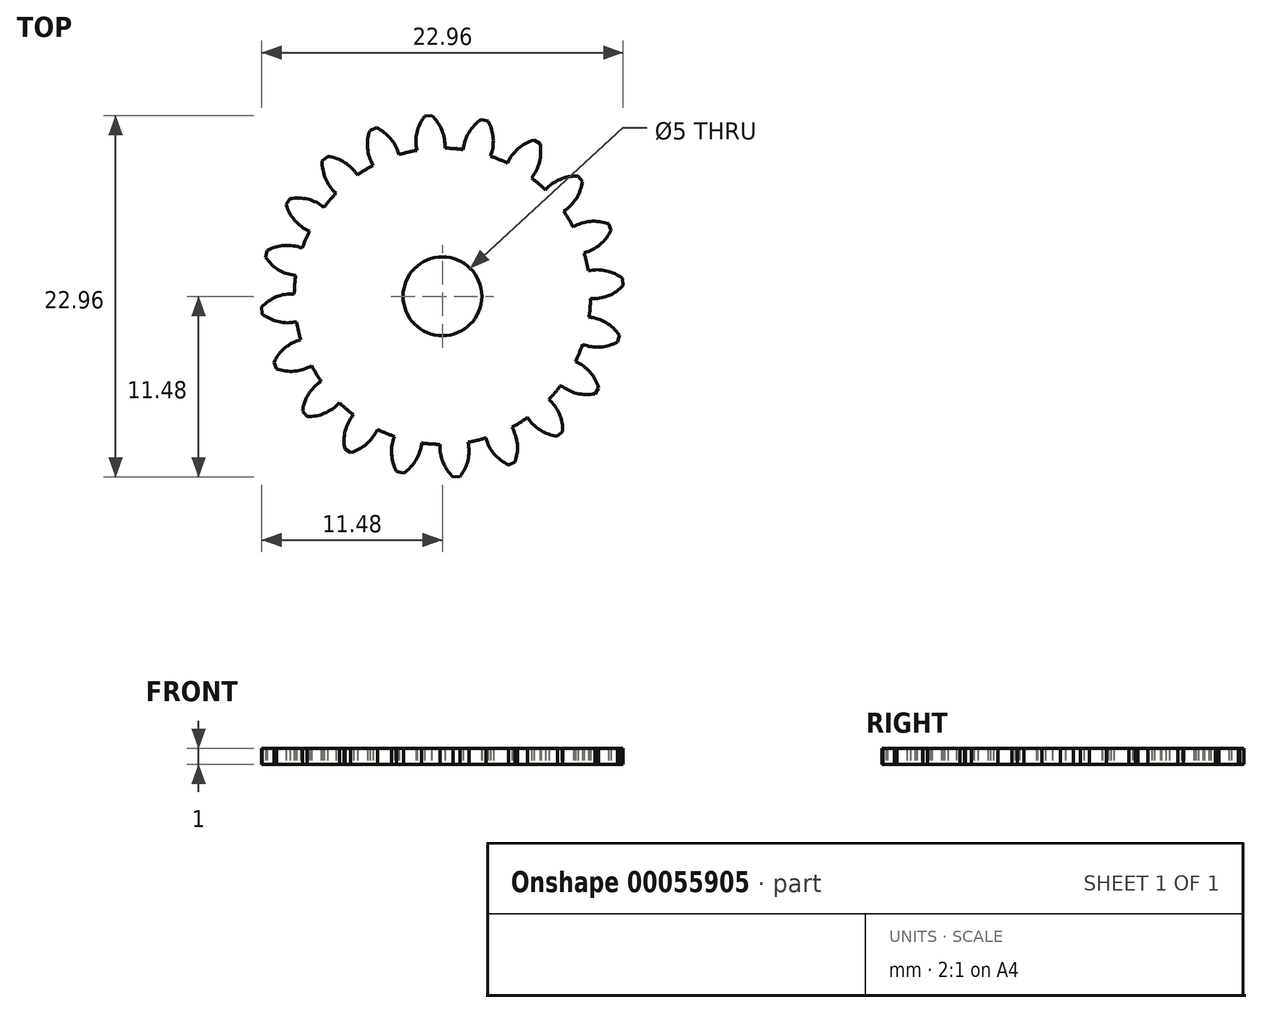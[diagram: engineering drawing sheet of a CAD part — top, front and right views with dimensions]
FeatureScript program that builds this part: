
annotation { "Feature Type Name" : "Feature", "Feature Type Description" : "" }
export const myFeature = defineFeature(function(context is Context, id is Id, definition is map)
    precondition{}
    {
        {
            assignVariable(context, id + "F0", {"name" : "GearDepth", "anyValue" : 1});
        }
        {
            var Q0;
            Q0=qCreatedBy(makeId("Top.planeOp"),FACE);
            var sketch = newSketch(context, id + "F1", { "sketchPlane" : qUnion([Q0])});
            skCircle(sketch, "E0", {"center": v(0, 0) * mm, "radius": 9.4 * mm});
            skCircle(sketch, "E1", {"center": v(0, 0) * mm, "radius": 10.45 * mm, "construction": true});
            skCircle(sketch, "E2", {"center": v(0, 0) * mm, "radius": 11.5 * mm, "construction": true});
            skLineSegment(sketch, "E3", {"start": v(0, 0) * mm, "end": v(0, 17.6) * mm, "construction": true});
            skLineSegment(sketch, "E4", {"start": v(0, 0) * mm, "end": v(-1.42, 18) * mm, "construction": true});
            skLineSegment(sketch, "E5", {"start": v(0, 10.45) * mm, "end": v(-10.54, 10.45) * mm, "construction": true});
            skLineSegment(sketch, "E6", {"start": v(0, 10.45) * mm, "end": v(-10.3, 6.7) * mm, "construction": true});
            skCircle(sketch, "E7", {"center": v(0, 10.45) * mm, "radius": 2.61 * mm, "construction": true});
            skCircle(sketch, "E8", {"center": v(-2.46, 9.56) * mm, "radius": 2.61 * mm, "construction": true});
            skArc(sketch, "E9", {"start": v(-4.91, 10.45) * mm, "mid": v(-4.92, 10.42) * mm, "end": v(-4.94, 10.39) * mm});
            skArc(sketch, "E10.trimOffspring", {"start": v(0.15, 9.4) * mm, "mid": v(-0.03, 10.54) * mm, "end": v(-0.68, 11.48) * mm});
            skArc(sketch, "E11.MirrorCS", {"start": v(-1.62, 9.27) * mm, "mid": v(-1.62, 10.41) * mm, "end": v(-1.12, 11.45) * mm});
            skLineSegment(sketch, "E12", {"start": v(-1.12, 11.45) * mm, "end": v(-0.68, 11.48) * mm});
            skArc(sketch, "E13.1.0", {"start": v(-2.76, 9) * mm, "mid": v(-3.29, 10.01) * mm, "end": v(-4.2, 10.7) * mm});
            skLineSegment(sketch, "E13.1.1", {"start": v(-4.6, 10.54) * mm, "end": v(-4.2, 10.7) * mm});
            skArc(sketch, "E13.1.2", {"start": v(-4.4, 8.31) * mm, "mid": v(-4.76, 9.4) * mm, "end": v(-4.6, 10.54) * mm});
            skArc(sketch, "E13.2.0", {"start": v(-5.4, 7.7) * mm, "mid": v(-6.22, 8.5) * mm, "end": v(-7.3, 8.89) * mm});
            skLineSegment(sketch, "E13.2.1", {"start": v(-7.64, 8.6) * mm, "end": v(-7.3, 8.89) * mm});
            skArc(sketch, "E13.2.2", {"start": v(-6.76, 6.54) * mm, "mid": v(-7.43, 7.47) * mm, "end": v(-7.64, 8.6) * mm});
            skArc(sketch, "E13.3.0", {"start": v(-7.52, 5.65) * mm, "mid": v(-8.54, 6.17) * mm, "end": v(-9.69, 6.2) * mm});
            skLineSegment(sketch, "E13.3.1", {"start": v(-9.92, 5.82) * mm, "end": v(-9.69, 6.2) * mm});
            skArc(sketch, "E13.3.2", {"start": v(-8.45, 4.13) * mm, "mid": v(-9.37, 4.81) * mm, "end": v(-9.92, 5.82) * mm});
            skArc(sketch, "E13.4.0", {"start": v(-8.9, 3.05) * mm, "mid": v(-10.03, 3.23) * mm, "end": v(-11.13, 2.9) * mm});
            skLineSegment(sketch, "E13.4.1", {"start": v(-11.23, 2.47) * mm, "end": v(-11.13, 2.9) * mm});
            skArc(sketch, "E13.4.2", {"start": v(-9.32, 1.32) * mm, "mid": v(-10.4, 1.68) * mm, "end": v(-11.23, 2.47) * mm});
            skArc(sketch, "E13.5.0", {"start": v(-9.4, 0.15) * mm, "mid": v(-10.54, -0.03) * mm, "end": v(-11.48, -0.68) * mm});
            skLineSegment(sketch, "E13.5.1", {"start": v(-11.45, -1.12) * mm, "end": v(-11.48, -0.68) * mm});
            skArc(sketch, "E13.5.2", {"start": v(-9.27, -1.62) * mm, "mid": v(-10.41, -1.62) * mm, "end": v(-11.45, -1.12) * mm});
            skArc(sketch, "E13.6.0", {"start": v(-9, -2.76) * mm, "mid": v(-10.01, -3.29) * mm, "end": v(-10.7, -4.2) * mm});
            skLineSegment(sketch, "E13.6.1", {"start": v(-10.54, -4.6) * mm, "end": v(-10.7, -4.2) * mm});
            skArc(sketch, "E13.6.2", {"start": v(-8.31, -4.4) * mm, "mid": v(-9.4, -4.76) * mm, "end": v(-10.54, -4.6) * mm});
            skArc(sketch, "E13.7.0", {"start": v(-7.7, -5.4) * mm, "mid": v(-8.5, -6.22) * mm, "end": v(-8.89, -7.3) * mm});
            skLineSegment(sketch, "E13.7.1", {"start": v(-8.6, -7.64) * mm, "end": v(-8.89, -7.3) * mm});
            skArc(sketch, "E13.7.2", {"start": v(-6.54, -6.76) * mm, "mid": v(-7.47, -7.43) * mm, "end": v(-8.6, -7.64) * mm});
            skArc(sketch, "E13.8.0", {"start": v(-5.65, -7.52) * mm, "mid": v(-6.17, -8.54) * mm, "end": v(-6.2, -9.69) * mm});
            skLineSegment(sketch, "E13.8.1", {"start": v(-5.82, -9.92) * mm, "end": v(-6.2, -9.69) * mm});
            skArc(sketch, "E13.8.2", {"start": v(-4.13, -8.45) * mm, "mid": v(-4.81, -9.37) * mm, "end": v(-5.82, -9.92) * mm});
            skArc(sketch, "E13.9.0", {"start": v(-3.05, -8.9) * mm, "mid": v(-3.23, -10.03) * mm, "end": v(-2.9, -11.13) * mm});
            skLineSegment(sketch, "E13.9.1", {"start": v(-2.47, -11.23) * mm, "end": v(-2.9, -11.13) * mm});
            skArc(sketch, "E13.9.2", {"start": v(-1.32, -9.32) * mm, "mid": v(-1.68, -10.4) * mm, "end": v(-2.47, -11.23) * mm});
            skArc(sketch, "E13.10.0", {"start": v(-0.15, -9.4) * mm, "mid": v(0.03, -10.54) * mm, "end": v(0.68, -11.48) * mm});
            skLineSegment(sketch, "E13.10.1", {"start": v(1.12, -11.45) * mm, "end": v(0.68, -11.48) * mm});
            skArc(sketch, "E13.10.2", {"start": v(1.62, -9.27) * mm, "mid": v(1.62, -10.41) * mm, "end": v(1.12, -11.45) * mm});
            skArc(sketch, "E13.11.0", {"start": v(2.76, -9) * mm, "mid": v(3.29, -10.01) * mm, "end": v(4.2, -10.7) * mm});
            skLineSegment(sketch, "E13.11.1", {"start": v(4.6, -10.54) * mm, "end": v(4.2, -10.7) * mm});
            skArc(sketch, "E13.11.2", {"start": v(4.4, -8.31) * mm, "mid": v(4.76, -9.4) * mm, "end": v(4.6, -10.54) * mm});
            skArc(sketch, "E13.12.0", {"start": v(5.4, -7.7) * mm, "mid": v(6.22, -8.5) * mm, "end": v(7.3, -8.89) * mm});
            skLineSegment(sketch, "E13.12.1", {"start": v(7.64, -8.6) * mm, "end": v(7.3, -8.89) * mm});
            skArc(sketch, "E13.12.2", {"start": v(6.76, -6.54) * mm, "mid": v(7.43, -7.47) * mm, "end": v(7.64, -8.6) * mm});
            skArc(sketch, "E13.13.0", {"start": v(7.52, -5.65) * mm, "mid": v(8.54, -6.17) * mm, "end": v(9.69, -6.2) * mm});
            skLineSegment(sketch, "E13.13.1", {"start": v(9.92, -5.82) * mm, "end": v(9.69, -6.2) * mm});
            skArc(sketch, "E13.13.2", {"start": v(8.45, -4.13) * mm, "mid": v(9.37, -4.81) * mm, "end": v(9.92, -5.82) * mm});
            skArc(sketch, "E13.14.0", {"start": v(8.9, -3.05) * mm, "mid": v(10.03, -3.23) * mm, "end": v(11.13, -2.9) * mm});
            skLineSegment(sketch, "E13.14.1", {"start": v(11.23, -2.47) * mm, "end": v(11.13, -2.9) * mm});
            skArc(sketch, "E13.14.2", {"start": v(9.32, -1.32) * mm, "mid": v(10.4, -1.68) * mm, "end": v(11.23, -2.47) * mm});
            skArc(sketch, "E13.15.0", {"start": v(9.4, -0.15) * mm, "mid": v(10.54, 0.03) * mm, "end": v(11.48, 0.68) * mm});
            skLineSegment(sketch, "E13.15.1", {"start": v(11.45, 1.12) * mm, "end": v(11.48, 0.68) * mm});
            skArc(sketch, "E13.15.2", {"start": v(9.27, 1.62) * mm, "mid": v(10.41, 1.62) * mm, "end": v(11.45, 1.12) * mm});
            skArc(sketch, "E13.16.0", {"start": v(9, 2.76) * mm, "mid": v(10.01, 3.29) * mm, "end": v(10.7, 4.2) * mm});
            skLineSegment(sketch, "E13.16.1", {"start": v(10.54, 4.6) * mm, "end": v(10.7, 4.2) * mm});
            skArc(sketch, "E13.16.2", {"start": v(8.31, 4.4) * mm, "mid": v(9.4, 4.76) * mm, "end": v(10.54, 4.6) * mm});
            skArc(sketch, "E13.17.0", {"start": v(7.7, 5.4) * mm, "mid": v(8.5, 6.22) * mm, "end": v(8.89, 7.3) * mm});
            skLineSegment(sketch, "E13.17.1", {"start": v(8.6, 7.64) * mm, "end": v(8.89, 7.3) * mm});
            skArc(sketch, "E13.17.2", {"start": v(6.54, 6.76) * mm, "mid": v(7.47, 7.43) * mm, "end": v(8.6, 7.64) * mm});
            skArc(sketch, "E13.18.0", {"start": v(5.65, 7.52) * mm, "mid": v(6.17, 8.54) * mm, "end": v(6.2, 9.69) * mm});
            skLineSegment(sketch, "E13.18.1", {"start": v(5.82, 9.92) * mm, "end": v(6.2, 9.69) * mm});
            skArc(sketch, "E13.18.2", {"start": v(4.13, 8.45) * mm, "mid": v(4.81, 9.37) * mm, "end": v(5.82, 9.92) * mm});
            skArc(sketch, "E13.19.0", {"start": v(3.05, 8.9) * mm, "mid": v(3.23, 10.03) * mm, "end": v(2.9, 11.13) * mm});
            skLineSegment(sketch, "E13.19.1", {"start": v(2.47, 11.23) * mm, "end": v(2.9, 11.13) * mm});
            skArc(sketch, "E13.19.2", {"start": v(1.32, 9.32) * mm, "mid": v(1.68, 10.4) * mm, "end": v(2.47, 11.23) * mm});
            skCircle(sketch, "E14", {"center": v(0, 0) * mm, "radius": 2.5 * mm});
            skSolve(sketch);
        }
        {
            var Q0;
            {var subQ0=sQuery(id+"F1.wireOp",EDGE,"E10.trimOffspring");Q0=makeQuery(id+"F1.imprint","IMPRINT",FACE,{"disambiguationData":[TD([[makeQuery(id+"F1.imprint","IMPRINT",EDGE,{"derivedFrom":subQ0}),1.0]])]});}
            var Q1;
            {var subQ0=sQuery(id+"F1.wireOp",EDGE,"E0");var subQ1=makeQuery(id+"F1.imprint","INTERSECT",VERTEX,{"derivedFrom":[subQ0,sQuery(id+"F1.wireOp",EDGE,"E10.trimOffspring")]});Q1=makeQuery(id+"F1.imprint","IMPRINT",FACE,{"disambiguationData":[TD([[makeQuery(id+"F1.imprint","IMPRINT",EDGE,{"disambiguationData":[TD([[subQ1,-1.0]])],"derivedFrom":subQ0}),1.0]])]});}
            var Q2;
            {var subQ0=sQuery(id+"F1.wireOp",EDGE,"E13.1.0");Q2=makeQuery(id+"F1.imprint","IMPRINT",FACE,{"disambiguationData":[TD([[makeQuery(id+"F1.imprint","IMPRINT",EDGE,{"derivedFrom":subQ0}),1.0]])]});}
            var Q3;
            {var subQ0=sQuery(id+"F1.wireOp",EDGE,"E13.2.0");Q3=makeQuery(id+"F1.imprint","IMPRINT",FACE,{"disambiguationData":[TD([[makeQuery(id+"F1.imprint","IMPRINT",EDGE,{"derivedFrom":subQ0}),1.0]])]});}
            var Q4;
            {var subQ0=sQuery(id+"F1.wireOp",EDGE,"E13.3.0");Q4=makeQuery(id+"F1.imprint","IMPRINT",FACE,{"disambiguationData":[TD([[makeQuery(id+"F1.imprint","IMPRINT",EDGE,{"derivedFrom":subQ0}),1.0]])]});}
            var Q5;
            {var subQ0=sQuery(id+"F1.wireOp",EDGE,"E13.4.0");Q5=makeQuery(id+"F1.imprint","IMPRINT",FACE,{"disambiguationData":[TD([[makeQuery(id+"F1.imprint","IMPRINT",EDGE,{"derivedFrom":subQ0}),1.0]])]});}
            var Q6;
            {var subQ0=sQuery(id+"F1.wireOp",EDGE,"E13.5.0");Q6=makeQuery(id+"F1.imprint","IMPRINT",FACE,{"disambiguationData":[TD([[makeQuery(id+"F1.imprint","IMPRINT",EDGE,{"derivedFrom":subQ0}),1.0]])]});}
            var Q7;
            {var subQ0=sQuery(id+"F1.wireOp",EDGE,"E13.6.0");Q7=makeQuery(id+"F1.imprint","IMPRINT",FACE,{"disambiguationData":[TD([[makeQuery(id+"F1.imprint","IMPRINT",EDGE,{"derivedFrom":subQ0}),1.0]])]});}
            var Q8;
            {var subQ0=sQuery(id+"F1.wireOp",EDGE,"E13.7.0");Q8=makeQuery(id+"F1.imprint","IMPRINT",FACE,{"disambiguationData":[TD([[makeQuery(id+"F1.imprint","IMPRINT",EDGE,{"derivedFrom":subQ0}),1.0]])]});}
            var Q9;
            {var subQ0=sQuery(id+"F1.wireOp",EDGE,"E13.8.0");Q9=makeQuery(id+"F1.imprint","IMPRINT",FACE,{"disambiguationData":[TD([[makeQuery(id+"F1.imprint","IMPRINT",EDGE,{"derivedFrom":subQ0}),1.0]])]});}
            var Q10;
            {var subQ0=sQuery(id+"F1.wireOp",EDGE,"E13.9.0");Q10=makeQuery(id+"F1.imprint","IMPRINT",FACE,{"disambiguationData":[TD([[makeQuery(id+"F1.imprint","IMPRINT",EDGE,{"derivedFrom":subQ0}),1.0]])]});}
            var Q11;
            {var subQ0=sQuery(id+"F1.wireOp",EDGE,"E13.10.0");Q11=makeQuery(id+"F1.imprint","IMPRINT",FACE,{"disambiguationData":[TD([[makeQuery(id+"F1.imprint","IMPRINT",EDGE,{"derivedFrom":subQ0}),1.0]])]});}
            var Q12;
            {var subQ0=sQuery(id+"F1.wireOp",EDGE,"E13.11.0");Q12=makeQuery(id+"F1.imprint","IMPRINT",FACE,{"disambiguationData":[TD([[makeQuery(id+"F1.imprint","IMPRINT",EDGE,{"derivedFrom":subQ0}),1.0]])]});}
            var Q13;
            {var subQ0=sQuery(id+"F1.wireOp",EDGE,"E13.12.0");Q13=makeQuery(id+"F1.imprint","IMPRINT",FACE,{"disambiguationData":[TD([[makeQuery(id+"F1.imprint","IMPRINT",EDGE,{"derivedFrom":subQ0}),1.0]])]});}
            var Q14;
            {var subQ0=sQuery(id+"F1.wireOp",EDGE,"E13.13.0");Q14=makeQuery(id+"F1.imprint","IMPRINT",FACE,{"disambiguationData":[TD([[makeQuery(id+"F1.imprint","IMPRINT",EDGE,{"derivedFrom":subQ0}),1.0]])]});}
            var Q15;
            {var subQ0=sQuery(id+"F1.wireOp",EDGE,"E13.14.0");Q15=makeQuery(id+"F1.imprint","IMPRINT",FACE,{"disambiguationData":[TD([[makeQuery(id+"F1.imprint","IMPRINT",EDGE,{"derivedFrom":subQ0}),1.0]])]});}
            var Q16;
            {var subQ0=sQuery(id+"F1.wireOp",EDGE,"E13.15.0");Q16=makeQuery(id+"F1.imprint","IMPRINT",FACE,{"disambiguationData":[TD([[makeQuery(id+"F1.imprint","IMPRINT",EDGE,{"derivedFrom":subQ0}),1.0]])]});}
            var Q17;
            {var subQ0=sQuery(id+"F1.wireOp",EDGE,"E13.16.0");Q17=makeQuery(id+"F1.imprint","IMPRINT",FACE,{"disambiguationData":[TD([[makeQuery(id+"F1.imprint","IMPRINT",EDGE,{"derivedFrom":subQ0}),1.0]])]});}
            var Q18;
            {var subQ0=sQuery(id+"F1.wireOp",EDGE,"E13.17.0");Q18=makeQuery(id+"F1.imprint","IMPRINT",FACE,{"disambiguationData":[TD([[makeQuery(id+"F1.imprint","IMPRINT",EDGE,{"derivedFrom":subQ0}),1.0]])]});}
            var Q19;
            {var subQ0=sQuery(id+"F1.wireOp",EDGE,"E13.18.0");Q19=makeQuery(id+"F1.imprint","IMPRINT",FACE,{"disambiguationData":[TD([[makeQuery(id+"F1.imprint","IMPRINT",EDGE,{"derivedFrom":subQ0}),1.0]])]});}
            var Q20;
            {var subQ0=sQuery(id+"F1.wireOp",EDGE,"E13.19.0");Q20=makeQuery(id+"F1.imprint","IMPRINT",FACE,{"disambiguationData":[TD([[makeQuery(id+"F1.imprint","IMPRINT",EDGE,{"derivedFrom":subQ0}),1.0]])]});}
            var Q21;
            Q21=sQuery(id+"F1.wireOp",EDGE,"E0");
            var Q22;
            Q22=sQuery(id+"F1.wireOp",EDGE,"E10.trimOffspring");
            var Q23;
            Q23=sQuery(id+"F1.wireOp",EDGE,"E12");
            var Q24;
            Q24=sQuery(id+"F1.wireOp",EDGE,"E11.MirrorCS");
            extrude(context, id + "F2", {"entities" : qUnion([Q0, Q1, Q2, Q3, Q4, Q5, Q6, Q7, Q8, Q9, Q10, Q11, Q12, Q13, Q14, Q15, Q16, Q17, Q18, Q19, Q20]), "surfaceEntities" : qUnion([Q21, Q22, Q23, Q24]), "depth" : (getVariable(context, 'GearDepth')) * mm});
        }
    });
